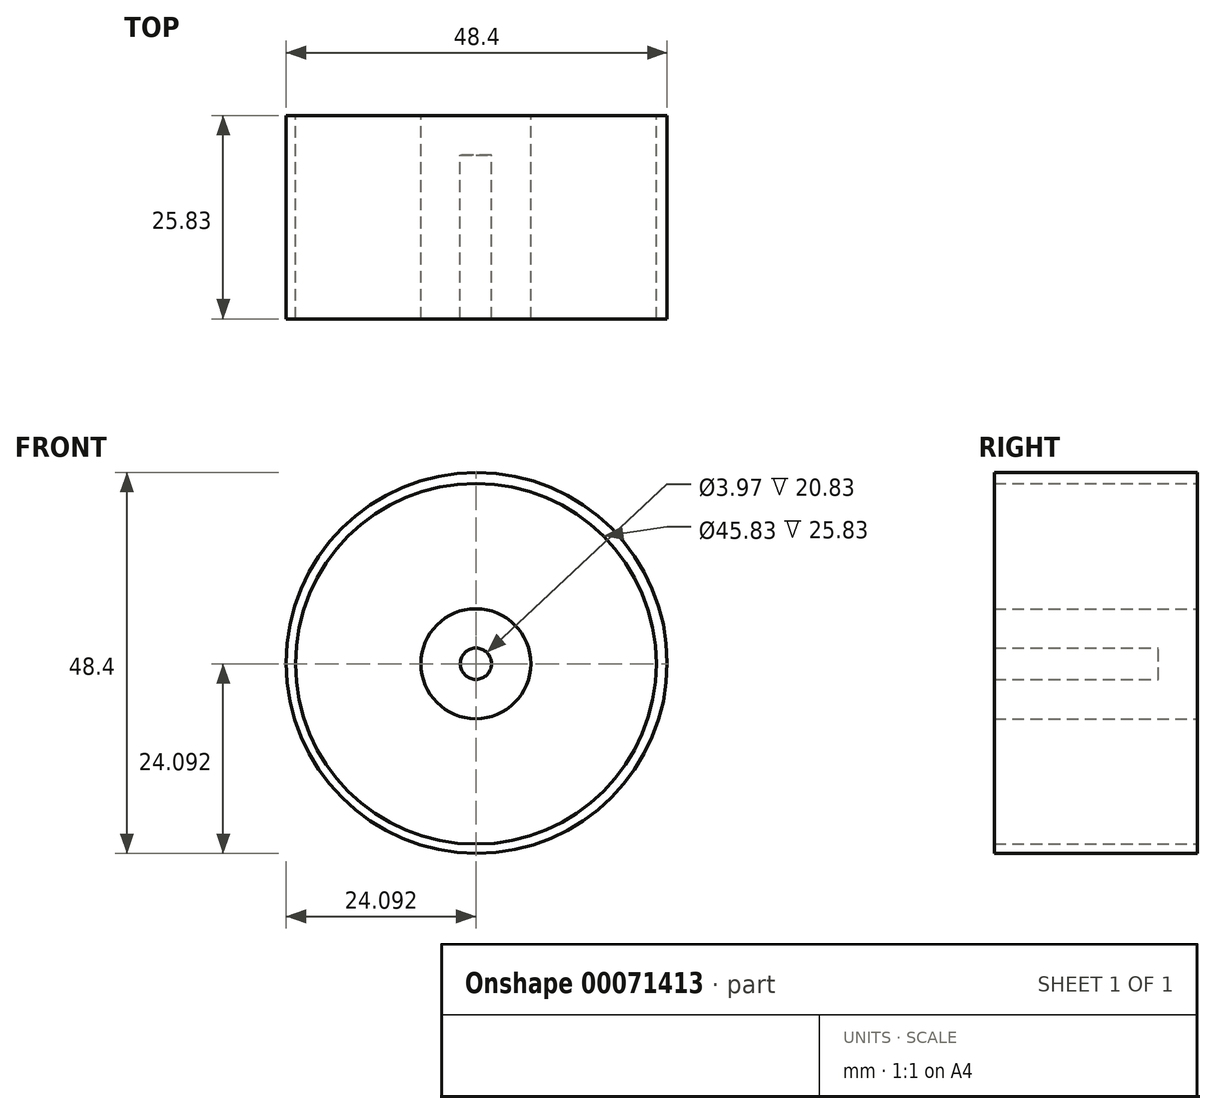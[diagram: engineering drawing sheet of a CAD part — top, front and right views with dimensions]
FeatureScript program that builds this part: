
annotation { "Feature Type Name" : "Feature", "Feature Type Description" : "" }
export const myFeature = defineFeature(function(context is Context, id is Id, definition is map)
    precondition{}
    {
        {
            var Q0;
            Q0=qCreatedBy(makeId("Front.planeOp"),FACE);
            var sketch = newSketch(context, id + "F0", { "sketchPlane" : qUnion([Q0])});
            skCircle(sketch, "E0", {"center": v(-0.1, -0.1) * mm, "radius": 22.92 * mm});
            skCircle(sketch, "E1", {"center": v(-0.1, -0.1) * mm, "radius": 6.99 * mm});
            skCircle(sketch, "E2", {"center": v(0, 0) * mm, "radius": 24.2 * mm});
            skLineSegment(sketch, "E3", {"start": v(-7.1, 0) * mm, "end": v(-23.02, 0) * mm});
            skLineSegment(sketch, "E4", {"start": v(0, 6.88) * mm, "end": v(0, 22.8) * mm});
            skLineSegment(sketch, "E5", {"start": v(6.88, 0) * mm, "end": v(22.8, 0) * mm});
            skLineSegment(sketch, "E6", {"start": v(0, -7.1) * mm, "end": v(0, -23.02) * mm});
            skLineSegment(sketch, "E7", {"start": v(-4.65, 5.2) * mm, "end": v(-15.31, 17.04) * mm});
            skLineSegment(sketch, "E8", {"start": v(5.2, 4.44) * mm, "end": v(16.72, 15.44) * mm});
            skLineSegment(sketch, "E9", {"start": v(5.04, -4.83) * mm, "end": v(15.86, -16.54) * mm});
            skLineSegment(sketch, "E10", {"start": v(-4.9, -5.2) * mm, "end": v(-16.08, -16.54) * mm});
            skSolve(sketch);
        }
        {
            var Q0;
            Q0=makeQuery(id+"F0.imprint","IMPRINT",FACE,{"disambiguationData":[TD([[makeQuery(id+"F0.imprint","IMPRINT",EDGE,{"derivedFrom":sQuery(id+"F0.wireOp",EDGE,"E0")}),-1.0]])]});
            extrude(context, id + "F1", {"entities" : qUnion([Q0]), "depth" : 25.83 * mm});
        }
        {
            var Q0;
            Q0=makeQuery(id+"F0.imprint","IMPRINT",FACE,{"disambiguationData":[TD([[makeQuery(id+"F0.imprint","IMPRINT",EDGE,{"derivedFrom":sQuery(id+"F0.wireOp",EDGE,"E1")}),1.0]])]});
            extrude(context, id + "F2", {"entities" : qUnion([Q0]), "depth" : 25.83 * mm});
        }
        {
            var Q0;
            Q0=makeQuery(id+"F2.opExtrude","CAP_FACE",FACE,{"disambiguationData":[OSD([sQuery(id+"F0.wireOp",EDGE,"E1")])],"isStart":false});
            shell(context, id + "F3", {"entities" : qUnion([Q0]), "thickness" : 5 * mm});
        }
    });
